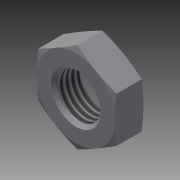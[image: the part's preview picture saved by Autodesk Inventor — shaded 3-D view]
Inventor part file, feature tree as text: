
AUTODESK INVENTOR PART (.ipt)
format: ipt  version: 2014 SP2 (Build 180246200, 246)  size: 156,672 bytes
history: native  units: in
note: dims shown in document units (in); Inventor stores cm internally (conversion verified against a paired STEP export)
features: other x70, sketch x3, revolve x2, extrude x1, thread x1
ambient origin geometry x8: Origin, YZ Plane, XZ Plane, XY Plane, X Axis, Y Axis, Z Axis, Center Point
bodies: Solid1 (feature_tree)
feature tree (77):
  sketch  "Sketch_8"  dims[d0=360.0deg d1=0.25in d2=0.0in]
  sketch  "Sketch_10"  dims[d3=360.0deg d4=0.1959in d5=0.0in]
  revolve  "Revolution1"  [1 undecoded]
  extrude  "Extrusion1"  Depth=0.1959in TaperAngle=0.0deg
  revolve  "Revolution2"  [1 undecoded]
  thread  "Thread1"  [1 undecoded]
  other  "NUT_XY"
  other  "NUT_YZ"
  other  "NUT_ZX"
  other  "NUT_X"
  other  "NUT_Y"
  other  "NUT_Z"
  other  "NUT_Center"
  other  "a1_XY"
  other  "a1_YZ"
  other  "a1_ZX"
  other  "a1_X"
  other  "a1_Y"
  other  "a1_Z"
  other  "a1_Center"
  other  "a2_XY"
  other  "a2_YZ"
  other  "a2_ZX"
  other  "a2_X"
  other  "a2_Y"
  other  "a2_Z"
  other  "a2_Center"
  other  "b1_XY"
  other  "b1_YZ"
  other  "b1_ZX"
  other  "b1_X"
  other  "b1_Y"
  other  "b1_Z"
  other  "b1_Center"
  other  "b2_XY"
  other  "b2_YZ"
  other  "b2_ZX"
  other  "b2_X"
  other  "b2_Y"
  other  "b2_Z"
  other  "b2_Center"
  other  "e_XY"
  other  "e_YZ"
  other  "e_ZX"
  other  "e_X"
  other  "e_Y"
  other  "e_Z"
  other  "e_Center"
  other  "ol1_XY"
  other  "ol1_YZ"
  other  "ol1_ZX"
  other  "ol1_X"
  other  "ol1_Y"
  other  "ol1_Z"
  other  "ol1_Center"
  other  "ol2_XY"
  other  "ol2_YZ"
  other  "ol2_ZX"
  other  "ol2_X"
  other  "ol2_Y"
  other  "ol2_Z"
  other  "ol2_Center"
  other  "th1_XY"
  other  "th1_YZ"
  other  "th1_ZX"
  other  "th1_X"
  other  "th1_Y"
  other  "th1_Z"
  other  "th1_Center"
  other  "th2_XY"
  other  "th2_YZ"
  other  "th2_ZX"
  other  "th2_X"
  other  "th2_Y"
  other  "th2_Z"
  other  "th2_Center"
  sketch  "Sketch_11"  dims[d6=0.0in d7=0.0in d8=0.0in]
note: 3 required parameter values undecoded (feature->parameter linkage not recoverable at this tier; creation-order binding heuristic only, values carry confidence <= 0.55)